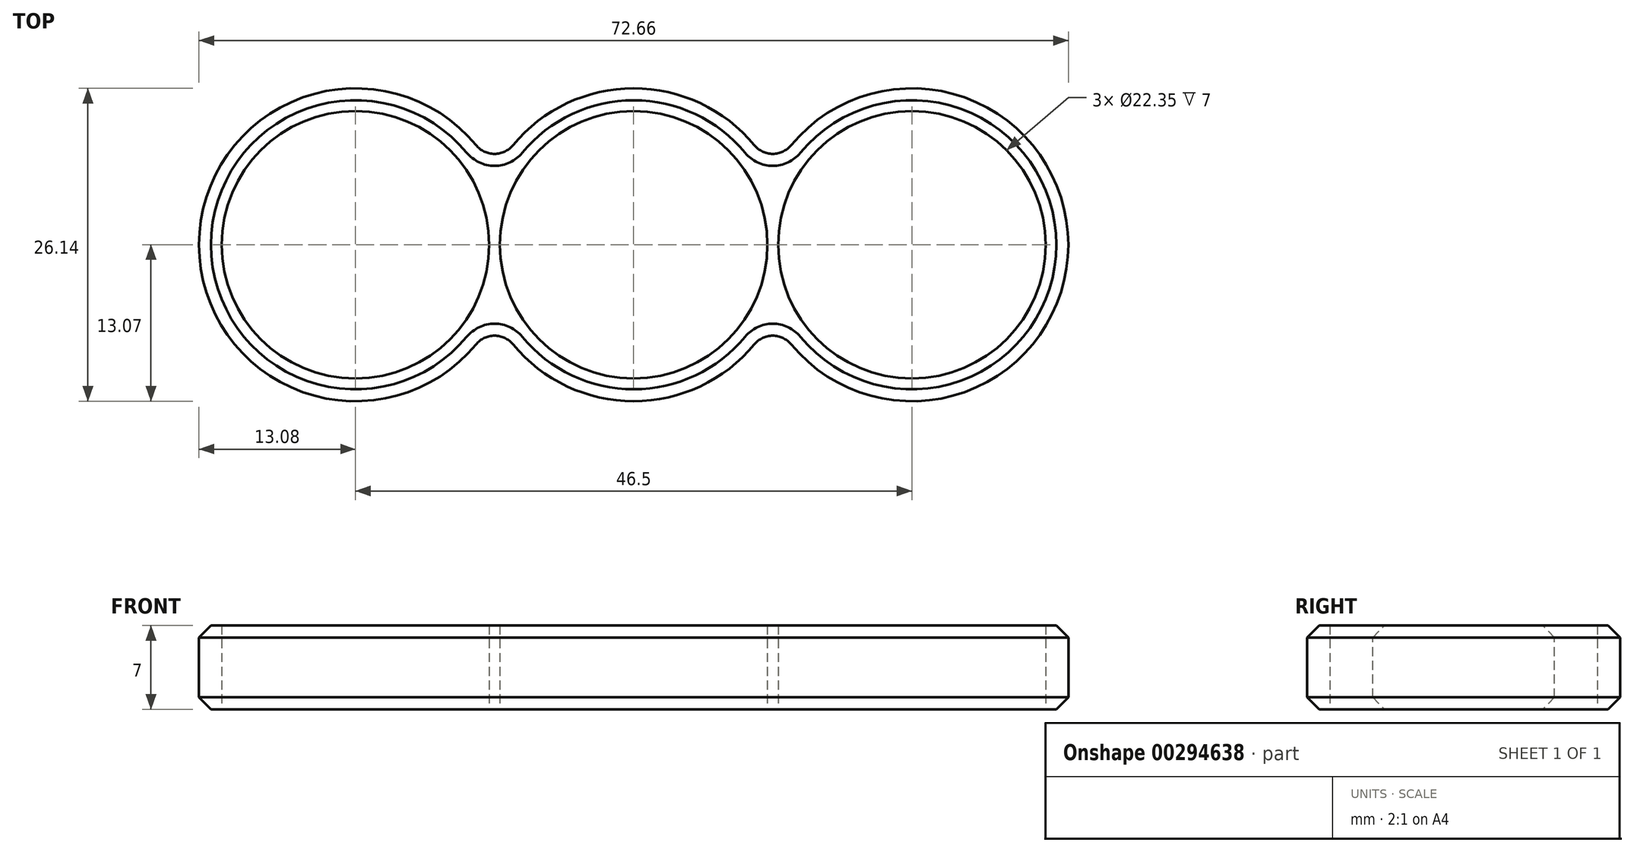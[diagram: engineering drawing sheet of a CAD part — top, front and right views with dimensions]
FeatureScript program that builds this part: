
annotation { "Feature Type Name" : "Feature", "Feature Type Description" : "" }
export const myFeature = defineFeature(function(context is Context, id is Id, definition is map)
    precondition{}
    {
        {
            var Q0;
            Q0=qCreatedBy(makeId("Top.planeOp"),FACE);
            var sketch = newSketch(context, id + "F0", { "sketchPlane" : qUnion([Q0])});
            skCircle(sketch, "E0", {"center": v(0, 0) * mm, "radius": 11.18 * mm});
            skCircle(sketch, "E1", {"center": v(-23.25, 0) * mm, "radius": 11.18 * mm});
            skCircle(sketch, "E2", {"center": v(23.25, 0) * mm, "radius": 11.18 * mm});
            skCircle(sketch, "E3", {"center": v(0, 0) * mm, "radius": 13.08 * mm});
            skCircle(sketch, "E4", {"center": v(23.25, 0) * mm, "radius": 13.08 * mm});
            skCircle(sketch, "E5", {"center": v(-23.25, 0) * mm, "radius": 13.08 * mm});
            skSolve(sketch);
        }
        {
            var Q0;
            {var subQ0=sQuery(id+"F0.wireOp",EDGE,"E3");var subQ1=sQuery(id+"F0.wireOp",EDGE,"E1");var subQ2=makeQuery(id+"F0.imprint","INTERSECT",VERTEX,{"disambiguationData":[OD(0.0)],"derivedFrom":[subQ1,subQ0]});Q0=makeQuery(id+"F0.imprint","IMPRINT",FACE,{"disambiguationData":[TD([[makeQuery(id+"F0.imprint","IMPRINT",EDGE,{"disambiguationData":[TD([[subQ2,-1.0]])],"derivedFrom":subQ1}),-1.0]])]});}
            var Q1;
            {var subQ0=sQuery(id+"F0.wireOp",EDGE,"E5");var subQ1=sQuery(id+"F0.wireOp",EDGE,"E0");var subQ2=makeQuery(id+"F0.imprint","INTERSECT",VERTEX,{"disambiguationData":[OD(0.0)],"derivedFrom":[subQ1,subQ0]});Q1=makeQuery(id+"F0.imprint","IMPRINT",FACE,{"disambiguationData":[TD([[makeQuery(id+"F0.imprint","IMPRINT",EDGE,{"disambiguationData":[TD([[subQ2,1.0]])],"derivedFrom":subQ1}),-1.0]])]});}
            var Q2;
            {var subQ0=sQuery(id+"F0.wireOp",EDGE,"E3");var subQ1=sQuery(id+"F0.wireOp",EDGE,"E2");var subQ2=makeQuery(id+"F0.imprint","INTERSECT",VERTEX,{"disambiguationData":[OD(0.0)],"derivedFrom":[subQ1,subQ0]});Q2=makeQuery(id+"F0.imprint","IMPRINT",FACE,{"disambiguationData":[TD([[makeQuery(id+"F0.imprint","IMPRINT",EDGE,{"disambiguationData":[TD([[subQ2,1.0]])],"derivedFrom":subQ1}),-1.0]])]});}
            var Q3;
            {var subQ0=sQuery(id+"F0.wireOp",EDGE,"E5");var subQ1=sQuery(id+"F0.wireOp",EDGE,"E0");var subQ2=makeQuery(id+"F0.imprint","INTERSECT",VERTEX,{"disambiguationData":[OD(1.0)],"derivedFrom":[subQ1,subQ0]});Q3=makeQuery(id+"F0.imprint","IMPRINT",FACE,{"disambiguationData":[TD([[makeQuery(id+"F0.imprint","IMPRINT",EDGE,{"disambiguationData":[TD([[subQ2,-1.0]])],"derivedFrom":subQ1}),-1.0]])]});}
            var Q4;
            {var subQ0=sQuery(id+"F0.wireOp",EDGE,"E4");var subQ5=sQuery(id+"F0.wireOp",EDGE,"E0");var subQ6=makeQuery(id+"F0.imprint","INTERSECT",VERTEX,{"disambiguationData":[OD(0.0)],"derivedFrom":[subQ5,subQ0]});Q4=makeQuery(id+"F0.imprint","IMPRINT",FACE,{"disambiguationData":[TD([[makeQuery(id+"F0.imprint","IMPRINT",EDGE,{"disambiguationData":[TD([[subQ6,1.0]])],"derivedFrom":subQ5}),-1.0]])]});}
            var Q5;
            {var subQ0=sQuery(id+"F0.wireOp",EDGE,"E5");var subQ5=sQuery(id+"F0.wireOp",EDGE,"E0");var subQ6=makeQuery(id+"F0.imprint","INTERSECT",VERTEX,{"disambiguationData":[OD(0.0)],"derivedFrom":[subQ5,subQ0]});Q5=makeQuery(id+"F0.imprint","IMPRINT",FACE,{"disambiguationData":[TD([[makeQuery(id+"F0.imprint","IMPRINT",EDGE,{"disambiguationData":[TD([[subQ6,-1.0]])],"derivedFrom":subQ5}),-1.0]])]});}
            extrude(context, id + "F1", {"entities" : qUnion([Q0, Q1, Q2, Q3, Q4, Q5]), "depth" : 7 * mm});
        }
        {
            var Q0;
            {var subQ0=sQuery(id+"F0.wireOp",EDGE,"E5");var subQ1=sQuery(id+"F0.wireOp",EDGE,"E3");Q0=makeQuery(id+"F1.opExtrude","SWEPT_EDGE",EDGE,{"disambiguationData":[OSD([subQ1,subQ0]),TDD([makeQuery(id+"F0.imprint","INTERSECT",VERTEX,{"disambiguationData":[OD(1.0)],"derivedFrom":[subQ1,subQ0]})])]});}
            var Q1;
            {var subQ0=sQuery(id+"F0.wireOp",EDGE,"E4");var subQ1=sQuery(id+"F0.wireOp",EDGE,"E3");Q1=makeQuery(id+"F1.opExtrude","SWEPT_EDGE",EDGE,{"disambiguationData":[OSD([subQ1,subQ0]),TDD([makeQuery(id+"F0.imprint","INTERSECT",VERTEX,{"disambiguationData":[OD(1.0)],"derivedFrom":[subQ1,subQ0]})])]});}
            var Q2;
            {var subQ0=sQuery(id+"F0.wireOp",EDGE,"E5");var subQ1=sQuery(id+"F0.wireOp",EDGE,"E3");Q2=makeQuery(id+"F1.opExtrude","SWEPT_EDGE",EDGE,{"disambiguationData":[OSD([subQ1,subQ0]),TDD([makeQuery(id+"F0.imprint","INTERSECT",VERTEX,{"disambiguationData":[OD(0.0)],"derivedFrom":[subQ1,subQ0]})])]});}
            var Q3;
            {var subQ0=sQuery(id+"F0.wireOp",EDGE,"E4");var subQ1=sQuery(id+"F0.wireOp",EDGE,"E3");Q3=makeQuery(id+"F1.opExtrude","SWEPT_EDGE",EDGE,{"disambiguationData":[OSD([subQ1,subQ0]),TDD([makeQuery(id+"F0.imprint","INTERSECT",VERTEX,{"disambiguationData":[OD(0.0)],"derivedFrom":[subQ1,subQ0]})])]});}
            fillet(context, id + "F2", {"entities" : qUnion([Q0, Q1, Q2, Q3]), "radius" : 2 * mm, "tangentPropagation" : true, "allowEdgeOverflow" : false});
        }
        {
            var Q0;
            {var subQ0=sQuery(id+"F0.wireOp",EDGE,"E3");Q0=makeQuery(id+"F1.opExtrude","CAP_EDGE",EDGE,{"disambiguationData":[OSD([subQ0]),TDD([makeQuery(id+"F0.imprint","IMPRINT",EDGE,{"disambiguationData":[TD([[makeQuery(id+"F0.imprint","INTERSECT",VERTEX,{"disambiguationData":[OD(1.0)],"derivedFrom":[subQ0,sQuery(id+"F0.wireOp",EDGE,"E5")]}),-1.0]])],"derivedFrom":subQ0})])],"isStart":false});}
            var Q1;
            Q1=makeQuery(id+"F1.opExtrude","CAP_EDGE",EDGE,{"disambiguationData":[OSD([sQuery(id+"F0.wireOp",EDGE,"E5")])],"isStart":true});
            chamfer(context, id + "F3", {"entities" : qUnion([Q0, Q1]), "width" : 1 * mm, "tangentPropagation" : true});
        }
    });
